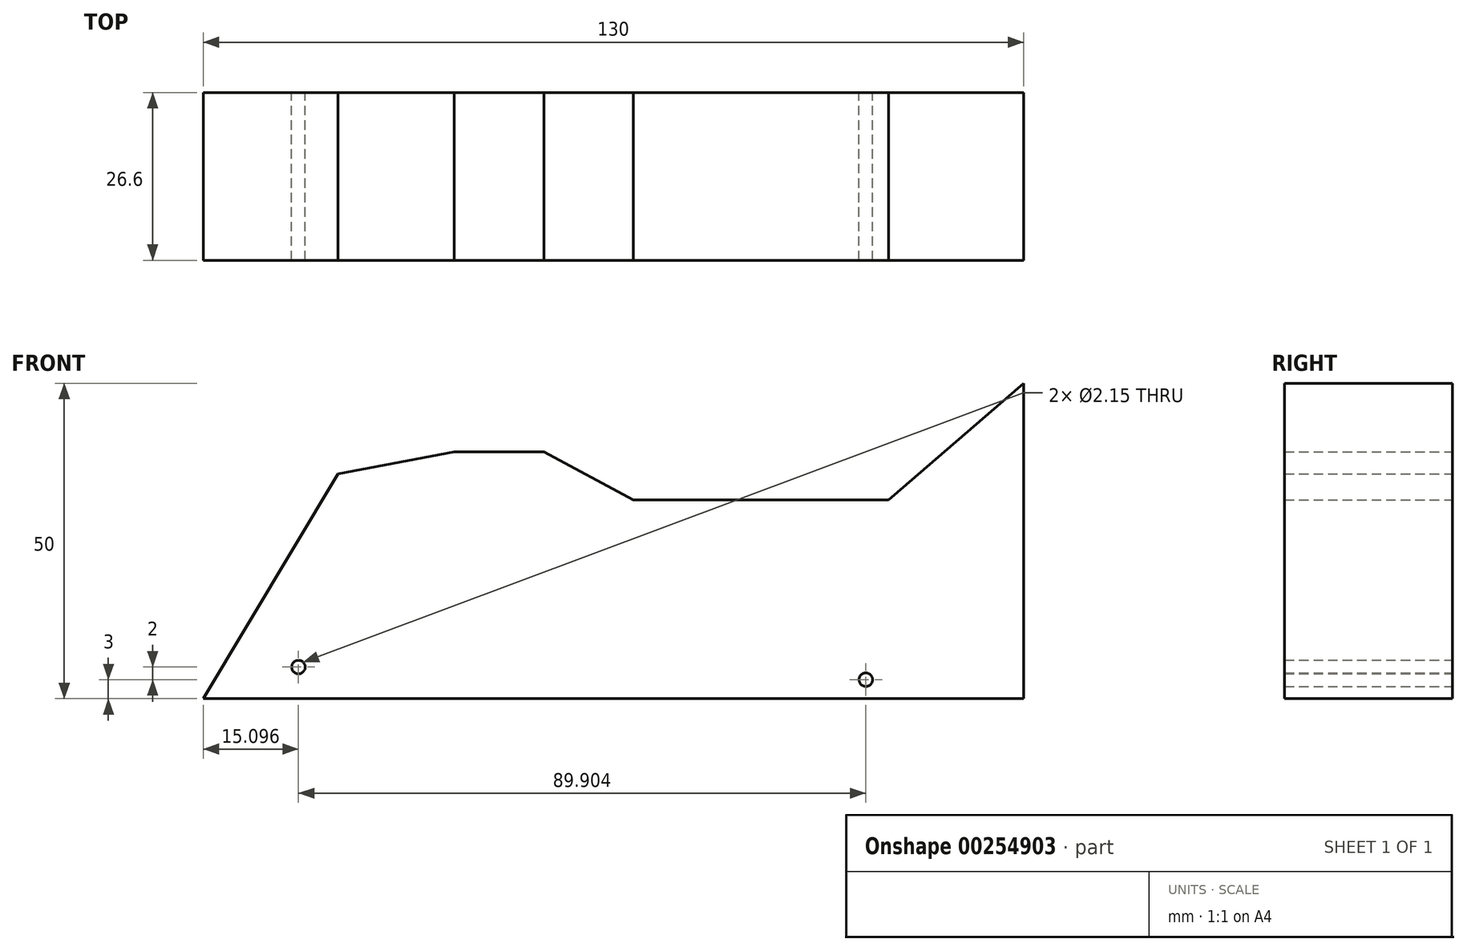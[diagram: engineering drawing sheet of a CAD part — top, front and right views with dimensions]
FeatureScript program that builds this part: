
annotation { "Feature Type Name" : "Feature", "Feature Type Description" : "" }
export const myFeature = defineFeature(function(context is Context, id is Id, definition is map)
    precondition{}
    {
        {
            var Q0;
            Q0=qCreatedBy(makeId("Front.planeOp"),FACE);
            var sketch = newSketch(context, id + "F0", { "sketchPlane" : qUnion([Q0])});
            skLineSegment(sketch, "E0.bottom", {"start": v(-50, 25) * mm, "end": v(50, 25) * mm});
            skLineSegment(sketch, "E0.top", {"start": v(-50, -25) * mm, "end": v(50, -25) * mm});
            skLineSegment(sketch, "E0.right", {"start": v(50, 25) * mm, "end": v(50, -25) * mm});
            skPoint(sketch, "E0.middle", {"position": v(0, 0) * mm});
            skLineSegment(sketch, "E1", {"start": v(-50, -25) * mm, "end": v(-80, -25) * mm});
            skLineSegment(sketch, "E2", {"start": v(-80, -25) * mm, "end": v(-50, 25) * mm});
            skLineSegment(sketch, "E3", {"start": v(25, -25) * mm, "end": v(50, -25) * mm});
            skPoint(sketch, "E4.end.orphan", {"position": v(-50, -16) * mm});
            skPoint(sketch, "E5.end.orphan", {"position": v(25, -22) * mm});
            skCircle(sketch, "E6", {"center": v(25, -22) * mm, "radius": 1.08 * mm});
            skCircle(sketch, "E7", {"center": v(-64.9, -20) * mm, "radius": 1.07 * mm});
            skSolve(sketch);
        }
        {
            var Q0;
            Q0=makeQuery(id+"F0.imprint","IMPRINT",FACE,{"disambiguationData":[TD([[makeQuery(id+"F0.imprint","IMPRINT",EDGE,{"derivedFrom":sQuery(id+"F0.wireOp",EDGE,"E0.bottom")}),-1.0]])]});
            extrude(context, id + "F1", {"entities" : qUnion([Q0]), "depth" : 26.6 * mm});
        }
        {
            var Q0;
            Q0=makeQuery(id+"F0.imprint","IMPRINT",FACE,{"disambiguationData":[TD([[makeQuery(id+"F0.imprint","IMPRINT",EDGE,{"derivedFrom":sQuery(id+"F0.wireOp",EDGE,"E7")}),1.0]])]});
            extrude(context, id + "F2", {"entities" : qUnion([Q0]), "operationType" : NewBodyOperationType.REMOVE, "endBound" : BoundingType.THROUGH_ALL, "oppositeDirection" : true, "depth" : 25 * mm});
        }
        {
            var Q0;
            Q0=makeQuery(id+"F1.opExtrude","CAP_FACE",FACE,{"disambiguationData":[OSD([sQuery(id+"F0.wireOp",EDGE,"E0.bottom"),sQuery(id+"F0.wireOp",EDGE,"E0.top"),sQuery(id+"F0.wireOp",EDGE,"E0.right"),sQuery(id+"F0.wireOp",EDGE,"E1"),sQuery(id+"F0.wireOp",EDGE,"E2"),sQuery(id+"F0.wireOp",EDGE,"E3"),sQuery(id+"F0.wireOp",EDGE,"E6"),sQuery(id+"F0.wireOp",EDGE,"E7")])],"isStart":true});
            var sketch = newSketch(context, id + "F3", { "sketchPlane" : qUnion([Q0])});
            skLineSegment(sketch, "E8", {"start": v(-50, 25) * mm, "end": v(-28.6, 6.5) * mm});
            skLineSegment(sketch, "E9", {"start": v(-28.6, 6.5) * mm, "end": v(11.84, 6.5) * mm});
            skLineSegment(sketch, "E10", {"start": v(11.84, 6.5) * mm, "end": v(26.04, 14.11) * mm});
            skLineSegment(sketch, "E11", {"start": v(26.04, 14.11) * mm, "end": v(40.23, 14.11) * mm});
            skLineSegment(sketch, "E12", {"start": v(40.23, 14.11) * mm, "end": v(58.63, 10.61) * mm});
            skSolve(sketch);
        }
        {
            var Q0;
            Q0=makeQuery(id+"F3.imprint","IMPRINT",FACE,{"disambiguationData":[TD([[makeQuery(id+"F3.imprint","IMPRINT",EDGE,{"derivedFrom":sQuery(id+"F3.wireOp",EDGE,"E8")}),1.0]])]});
            extrude(context, id + "F4", {"entities" : qUnion([Q0]), "operationType" : NewBodyOperationType.REMOVE, "endBound" : BoundingType.THROUGH_ALL, "oppositeDirection" : true, "depth" : 25 * mm});
        }
    });
